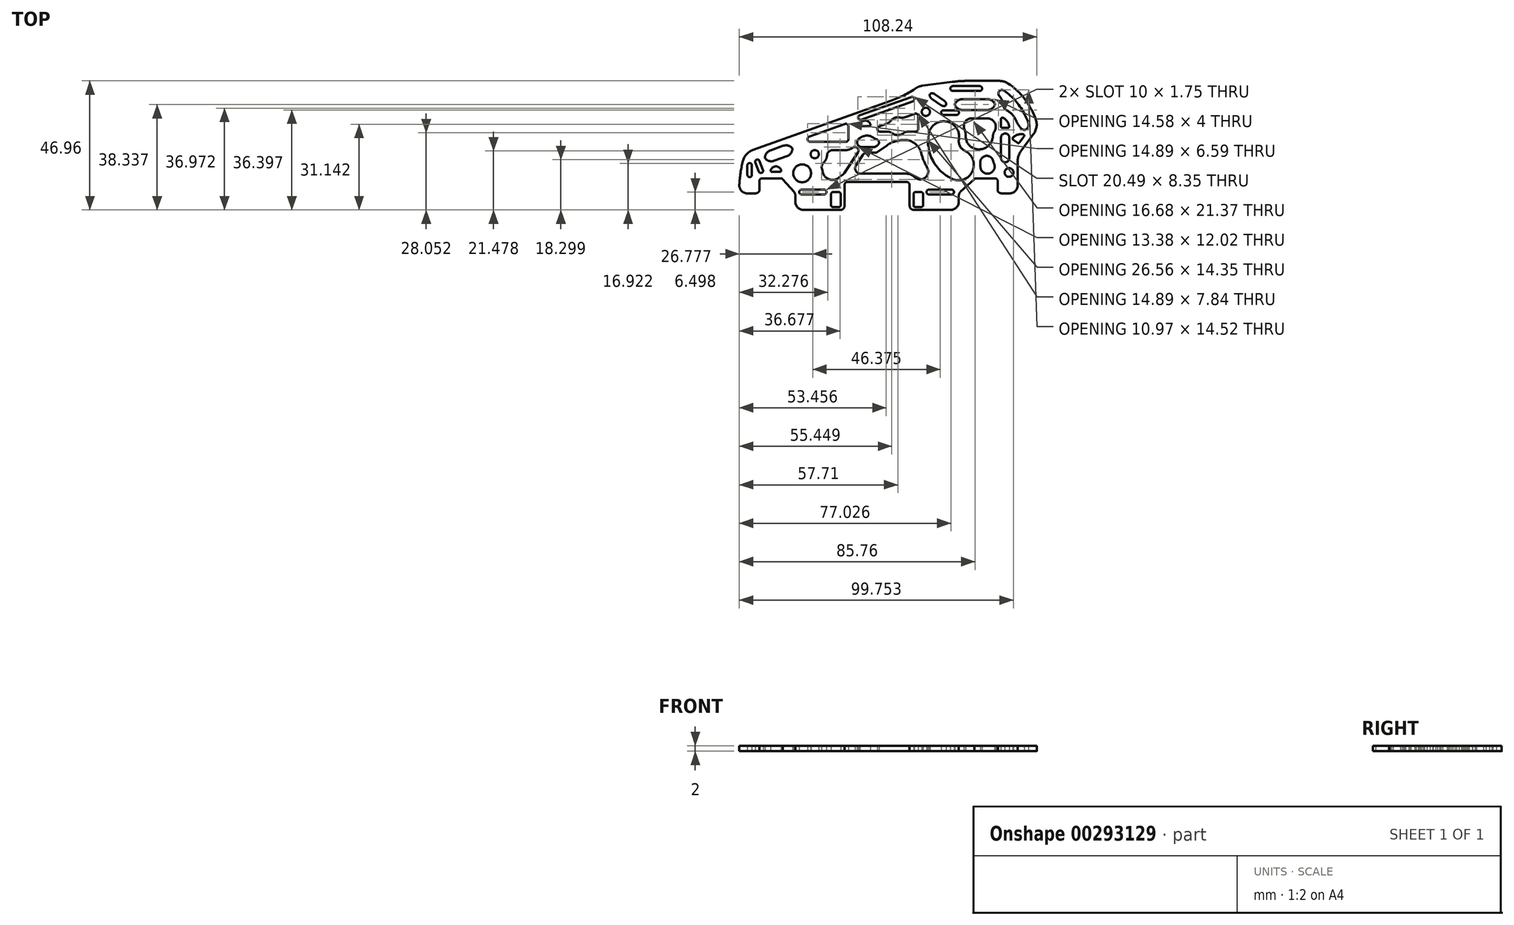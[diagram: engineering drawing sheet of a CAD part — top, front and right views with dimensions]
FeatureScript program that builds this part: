
annotation { "Feature Type Name" : "Feature", "Feature Type Description" : "" }
export const myFeature = defineFeature(function(context is Context, id is Id, definition is map)
    precondition{}
    {
        {
            var Q0;
            Q0=qCreatedBy(makeId("Top.planeOp"),FACE);
            var sketch = newSketch(context, id + "F0", { "sketchPlane" : qUnion([Q0])});
            skArc(sketch, "E0", {"start": v(29.13, 23.48) * mm, "mid": v(26.3, 23.4) * mm, "end": v(23.48, 23.12) * mm});
            skLineSegment(sketch, "E1", {"start": v(0.85, 16.15) * mm, "end": v(-49.03, -1.6) * mm});
            skArc(sketch, "E2", {"start": v(-49.03, -1.6) * mm, "mid": v(-51.49, -3.25) * mm, "end": v(-52.86, -5.87) * mm});
            skArc(sketch, "E3", {"start": v(-52.86, -5.87) * mm, "mid": v(-53.67, -10.05) * mm, "end": v(-54.12, -14.3) * mm});
            skArc(sketch, "E4", {"start": v(-54.12, -14.3) * mm, "mid": v(-53.31, -16.53) * mm, "end": v(-51.12, -17.48) * mm});
            skLineSegment(sketch, "E5", {"start": v(-51.12, -17.48) * mm, "end": v(-48.44, -17.48) * mm});
            skArc(sketch, "E6", {"start": v(-48.44, -17.48) * mm, "mid": v(-47.78, -17.37) * mm, "end": v(-47.2, -17.05) * mm});
            skArc(sketch, "E7", {"start": v(-47.2, -17.05) * mm, "mid": v(-46.92, -16.7) * mm, "end": v(-46.82, -16.27) * mm});
            skLineSegment(sketch, "E8", {"start": v(-46.82, -16.27) * mm, "end": v(-46.82, -12.98) * mm});
            skArc(sketch, "E9", {"start": v(-45.82, -11.98) * mm, "mid": v(-46.53, -12.27) * mm, "end": v(-46.82, -12.98) * mm});
            skLineSegment(sketch, "E10", {"start": v(-45.82, -11.98) * mm, "end": v(-39.02, -11.98) * mm});
            skArc(sketch, "E11", {"start": v(-38.23, -12.37) * mm, "mid": v(-38.58, -12.08) * mm, "end": v(-39.02, -11.98) * mm});
            skArc(sketch, "E12", {"start": v(-33.72, -20.48) * mm, "mid": v(-32.84, -22.6) * mm, "end": v(-30.72, -23.48) * mm});
            skLineSegment(sketch, "E13", {"start": v(-30.72, -23.48) * mm, "end": v(-17.32, -23.48) * mm});
            skArc(sketch, "E14", {"start": v(22.78, -23.48) * mm, "mid": v(24.9, -22.6) * mm, "end": v(25.78, -20.48) * mm});
            skLineSegment(sketch, "E15", {"start": v(25.78, -20.48) * mm, "end": v(25.78, -18.36) * mm});
            skArc(sketch, "E16", {"start": v(32.11, -11.98) * mm, "mid": v(31.73, -12.06) * mm, "end": v(31.4, -12.27) * mm});
            skLineSegment(sketch, "E17", {"start": v(32.11, -11.98) * mm, "end": v(38.91, -11.98) * mm});
            skArc(sketch, "E18", {"start": v(39.91, -12.98) * mm, "mid": v(39.62, -12.27) * mm, "end": v(38.91, -11.98) * mm});
            skLineSegment(sketch, "E19", {"start": v(39.91, -12.98) * mm, "end": v(39.91, -16.65) * mm});
            skArc(sketch, "E20", {"start": v(39.91, -16.65) * mm, "mid": v(40.62, -17.26) * mm, "end": v(41.53, -17.48) * mm});
            skLineSegment(sketch, "E21", {"start": v(41.53, -17.48) * mm, "end": v(44.2, -17.48) * mm});
            skArc(sketch, "E22", {"start": v(44.2, -17.48) * mm, "mid": v(46.32, -16.6) * mm, "end": v(47.2, -14.48) * mm});
            skLineSegment(sketch, "E23", {"start": v(47.2, -14.48) * mm, "end": v(47.2, -5.72) * mm});
            skArc(sketch, "E24", {"start": v(-47.04, -9.52) * mm, "mid": v(-45.98, -10) * mm, "end": v(-45.5, -8.94) * mm});
            skLineSegment(sketch, "E25", {"start": v(-48.27, -6.25) * mm, "end": v(-47.04, -9.52) * mm});
            skArc(sketch, "E26", {"start": v(-46.73, -5.66) * mm, "mid": v(-47.8, -5.18) * mm, "end": v(-48.27, -6.25) * mm});
            skLineSegment(sketch, "E27", {"start": v(-45.5, -8.94) * mm, "end": v(-46.73, -5.66) * mm});
            skCircle(sketch, "E28", {"center": v(-26.66, -3.2) * mm, "radius": 1.5 * mm});
            skCircle(sketch, "E29", {"center": v(13.78, 12.22) * mm, "radius": 1.5 * mm});
            skArc(sketch, "E30", {"start": v(-34.78, -1.3) * mm, "mid": v(-34.81, -1.1) * mm, "end": v(-34.92, -0.92) * mm});
            skArc(sketch, "E31", {"start": v(-36.77, -3.92) * mm, "mid": v(-35.39, -2.9) * mm, "end": v(-34.78, -1.3) * mm});
            skLineSegment(sketch, "E32", {"start": v(-41.48, -5.6) * mm, "end": v(-36.77, -3.92) * mm});
            skArc(sketch, "E33", {"start": v(-44.68, -4.82) * mm, "mid": v(-43.2, -5.69) * mm, "end": v(-41.48, -5.6) * mm});
            skArc(sketch, "E34", {"start": v(-44.8, -4.44) * mm, "mid": v(-44.78, -4.65) * mm, "end": v(-44.68, -4.82) * mm});
            skArc(sketch, "E35", {"start": v(-42.82, -1.83) * mm, "mid": v(-44.2, -2.84) * mm, "end": v(-44.8, -4.44) * mm});
            skLineSegment(sketch, "E36", {"start": v(-38.11, -0.15) * mm, "end": v(-42.82, -1.83) * mm});
            skArc(sketch, "E37", {"start": v(-34.92, -0.92) * mm, "mid": v(-36.4, -0.06) * mm, "end": v(-38.11, -0.15) * mm});
            skLineSegment(sketch, "E38", {"start": v(27.14, 12.86) * mm, "end": v(36.14, 12.86) * mm});
            skArc(sketch, "E39", {"start": v(24.4, 14.66) * mm, "mid": v(25.5, 13.35) * mm, "end": v(27.14, 12.86) * mm});
            skArc(sketch, "E40", {"start": v(24.4, 15.06) * mm, "mid": v(24.35, 14.86) * mm, "end": v(24.4, 14.66) * mm});
            skArc(sketch, "E41", {"start": v(27.14, 16.86) * mm, "mid": v(25.5, 16.37) * mm, "end": v(24.4, 15.06) * mm});
            skLineSegment(sketch, "E42", {"start": v(36.14, 16.86) * mm, "end": v(27.14, 16.86) * mm});
            skArc(sketch, "E43", {"start": v(38.89, 15.06) * mm, "mid": v(37.78, 16.37) * mm, "end": v(36.14, 16.86) * mm});
            skArc(sketch, "E44", {"start": v(38.89, 14.66) * mm, "mid": v(38.93, 14.86) * mm, "end": v(38.89, 15.06) * mm});
            skArc(sketch, "E45", {"start": v(36.14, 12.86) * mm, "mid": v(37.78, 13.35) * mm, "end": v(38.89, 14.66) * mm});
            skArc(sketch, "E46", {"start": v(-15.4, 1.28) * mm, "mid": v(-14.7, 1.57) * mm, "end": v(-14.4, 2.28) * mm});
            skLineSegment(sketch, "E47", {"start": v(-28.3, 1.28) * mm, "end": v(-15.4, 1.28) * mm});
            skArc(sketch, "E48", {"start": v(-28.64, 3.22) * mm, "mid": v(-29.29, 2.1) * mm, "end": v(-28.3, 1.28) * mm});
            skLineSegment(sketch, "E49", {"start": v(-15.74, 7.81) * mm, "end": v(-28.64, 3.22) * mm});
            skArc(sketch, "E50", {"start": v(-14.4, 6.87) * mm, "mid": v(-14.82, 7.69) * mm, "end": v(-15.74, 7.81) * mm});
            skLineSegment(sketch, "E51", {"start": v(-14.4, 2.28) * mm, "end": v(-14.4, 6.87) * mm});
            skLineSegment(sketch, "E52", {"start": v(-19.97, -22.48) * mm, "end": v(-17.97, -22.48) * mm});
            skArc(sketch, "E53", {"start": v(-20.72, -21.73) * mm, "mid": v(-20.5, -22.26) * mm, "end": v(-19.97, -22.48) * mm});
            skLineSegment(sketch, "E54", {"start": v(-20.72, -17.73) * mm, "end": v(-20.72, -21.73) * mm});
            skArc(sketch, "E55", {"start": v(-19.97, -16.98) * mm, "mid": v(-20.5, -17.2) * mm, "end": v(-20.72, -17.73) * mm});
            skLineSegment(sketch, "E56", {"start": v(-17.97, -16.98) * mm, "end": v(-19.97, -16.98) * mm});
            skArc(sketch, "E57", {"start": v(-17.22, -17.73) * mm, "mid": v(-17.44, -17.2) * mm, "end": v(-17.97, -16.98) * mm});
            skLineSegment(sketch, "E58", {"start": v(-17.22, -21.73) * mm, "end": v(-17.22, -17.73) * mm});
            skArc(sketch, "E59", {"start": v(-17.97, -22.48) * mm, "mid": v(-17.44, -22.26) * mm, "end": v(-17.22, -21.73) * mm});
            skArc(sketch, "E60", {"start": v(14.9, -16.1) * mm, "mid": v(14.03, -16.98) * mm, "end": v(14.9, -17.86) * mm});
            skLineSegment(sketch, "E61", {"start": v(23.16, -16.1) * mm, "end": v(14.9, -16.1) * mm});
            skArc(sketch, "E62", {"start": v(23.16, -17.86) * mm, "mid": v(24.03, -16.98) * mm, "end": v(23.16, -16.1) * mm});
            skLineSegment(sketch, "E63", {"start": v(14.9, -17.86) * mm, "end": v(23.16, -17.86) * mm});
            skArc(sketch, "E64", {"start": v(-31.47, -16.1) * mm, "mid": v(-32.34, -16.98) * mm, "end": v(-31.47, -17.86) * mm});
            skLineSegment(sketch, "E65", {"start": v(-23.22, -16.1) * mm, "end": v(-31.47, -16.1) * mm});
            skArc(sketch, "E66", {"start": v(-23.22, -17.86) * mm, "mid": v(-22.34, -16.98) * mm, "end": v(-23.22, -16.1) * mm});
            skLineSegment(sketch, "E67", {"start": v(-31.47, -17.86) * mm, "end": v(-23.22, -17.86) * mm});
            skCircle(sketch, "E68", {"center": v(-31.24, -10.14) * mm, "radius": 3.25 * mm});
            skCircle(sketch, "E69", {"center": v(44.08, -9.86) * mm, "radius": 1.6 * mm});
            skLineSegment(sketch, "E70", {"start": v(6.78, -13.3) * mm, "end": v(-14.72, -13.3) * mm});
            skArc(sketch, "E71", {"start": v(7.88, -14.4) * mm, "mid": v(7.56, -13.63) * mm, "end": v(6.78, -13.3) * mm});
            skArc(sketch, "E72", {"start": v(-14.72, -13.3) * mm, "mid": v(-15.5, -13.63) * mm, "end": v(-15.82, -14.4) * mm});
            skLineSegment(sketch, "E73", {"start": v(10.03, -22.48) * mm, "end": v(12.03, -22.48) * mm});
            skArc(sketch, "E74", {"start": v(9.28, -21.73) * mm, "mid": v(9.5, -22.26) * mm, "end": v(10.03, -22.48) * mm});
            skLineSegment(sketch, "E75", {"start": v(9.28, -17.73) * mm, "end": v(9.28, -21.73) * mm});
            skArc(sketch, "E76", {"start": v(10.03, -16.98) * mm, "mid": v(9.5, -17.2) * mm, "end": v(9.28, -17.73) * mm});
            skLineSegment(sketch, "E77", {"start": v(12.03, -16.98) * mm, "end": v(10.03, -16.98) * mm});
            skArc(sketch, "E78", {"start": v(12.78, -17.73) * mm, "mid": v(12.56, -17.2) * mm, "end": v(12.03, -16.98) * mm});
            skLineSegment(sketch, "E79", {"start": v(12.78, -21.73) * mm, "end": v(12.78, -17.73) * mm});
            skArc(sketch, "E80", {"start": v(12.03, -22.48) * mm, "mid": v(12.56, -22.26) * mm, "end": v(12.78, -21.73) * mm});
            skLineSegment(sketch, "E81", {"start": v(41.64, 6.36) * mm, "end": v(43.6, 6.36) * mm});
            skArc(sketch, "E82", {"start": v(41.14, 6.86) * mm, "mid": v(41.29, 6.5) * mm, "end": v(41.64, 6.36) * mm});
            skLineSegment(sketch, "E83", {"start": v(41.14, 9.62) * mm, "end": v(41.14, 6.86) * mm});
            skArc(sketch, "E84", {"start": v(41.87, 10.07) * mm, "mid": v(41.38, 10.05) * mm, "end": v(41.14, 9.62) * mm});
            skArc(sketch, "E85", {"start": v(44.1, 6.92) * mm, "mid": v(43.37, 8.77) * mm, "end": v(41.87, 10.07) * mm});
            skArc(sketch, "E86", {"start": v(43.6, 6.36) * mm, "mid": v(43.98, 6.53) * mm, "end": v(44.1, 6.92) * mm});
            skLineSegment(sketch, "E87", {"start": v(41.14, 2.86) * mm, "end": v(41.14, -4.64) * mm});
            skArc(sketch, "E88", {"start": v(44.14, 2.86) * mm, "mid": v(42.64, 4.36) * mm, "end": v(41.14, 2.86) * mm});
            skLineSegment(sketch, "E89", {"start": v(44.14, -4.64) * mm, "end": v(44.14, 2.86) * mm});
            skArc(sketch, "E90", {"start": v(41.14, -4.64) * mm, "mid": v(42.64, -6.14) * mm, "end": v(44.14, -4.64) * mm});
            skLineSegment(sketch, "E91", {"start": v(-9.8, 9.36) * mm, "end": v(9.03, 16.07) * mm});
            skArc(sketch, "E92", {"start": v(-10.36, 10.92) * mm, "mid": v(-10.86, 9.86) * mm, "end": v(-9.8, 9.36) * mm});
            skLineSegment(sketch, "E93", {"start": v(8.48, 17.62) * mm, "end": v(-10.36, 10.92) * mm});
            skArc(sketch, "E94", {"start": v(9.03, 16.07) * mm, "mid": v(9.53, 17.12) * mm, "end": v(8.48, 17.62) * mm});
            skLineSegment(sketch, "E95", {"start": v(23.58, 19.82) * mm, "end": v(33.38, 19.82) * mm});
            skLineSegment(sketch, "E96", {"start": v(33.38, 21.57) * mm, "end": v(23.58, 21.57) * mm});
            skLineSegment(sketch, "E97", {"start": v(7.33, 5) * mm, "end": v(10.03, 5) * mm});
            skArc(sketch, "E98", {"start": v(-3.2, 6.94) * mm, "mid": v(-3.85, 5.82) * mm, "end": v(-2.87, 5) * mm});
            skLineSegment(sketch, "E99", {"start": v(9.7, 11.53) * mm, "end": v(6.07, 10.24) * mm});
            skArc(sketch, "E100", {"start": v(11.03, 10.59) * mm, "mid": v(10.61, 11.4) * mm, "end": v(9.7, 11.53) * mm});
            skLineSegment(sketch, "E101", {"start": v(11.03, 6) * mm, "end": v(11.03, 10.59) * mm});
            skArc(sketch, "E102", {"start": v(10.03, 5) * mm, "mid": v(10.74, 5.29) * mm, "end": v(11.03, 6) * mm});
            skLineSegment(sketch, "E103", {"start": v(-33.72, -18.24) * mm, "end": v(-33.72, -20.48) * mm});
            skLineSegment(sketch, "E104", {"start": v(-34.22, -16.91) * mm, "end": v(-38.23, -12.37) * mm});
            skArc(sketch, "E105", {"start": v(-33.72, -18.24) * mm, "mid": v(-33.85, -17.53) * mm, "end": v(-34.22, -16.91) * mm});
            skLineSegment(sketch, "E106", {"start": v(26.42, -16.89) * mm, "end": v(31.4, -12.27) * mm});
            skArc(sketch, "E107", {"start": v(26.42, -16.89) * mm, "mid": v(25.95, -17.55) * mm, "end": v(25.78, -18.36) * mm});
            skArc(sketch, "E108", {"start": v(-49.53, -7.24) * mm, "mid": v(-50.35, -6.41) * mm, "end": v(-51.18, -7.24) * mm});
            skLineSegment(sketch, "E109", {"start": v(-51.18, -10.74) * mm, "end": v(-51.18, -7.24) * mm});
            skArc(sketch, "E110", {"start": v(-51.18, -10.74) * mm, "mid": v(-50.35, -11.56) * mm, "end": v(-49.53, -10.74) * mm});
            skLineSegment(sketch, "E111", {"start": v(-49.53, -7.24) * mm, "end": v(-49.53, -10.74) * mm});
            skLineSegment(sketch, "E112", {"start": v(7.88, -14.4) * mm, "end": v(7.88, -21.98) * mm});
            skLineSegment(sketch, "E113", {"start": v(-15.82, -21.98) * mm, "end": v(-15.82, -14.4) * mm});
            skArc(sketch, "E114", {"start": v(-17.32, -23.48) * mm, "mid": v(-16.26, -23.04) * mm, "end": v(-15.82, -21.98) * mm});
            skLineSegment(sketch, "E115", {"start": v(9.38, -23.48) * mm, "end": v(22.78, -23.48) * mm});
            skArc(sketch, "E116", {"start": v(7.88, -21.98) * mm, "mid": v(8.32, -23.04) * mm, "end": v(9.38, -23.48) * mm});
            skLineSegment(sketch, "E117", {"start": v(23.48, 23.12) * mm, "end": v(12.54, 21.72) * mm});
            skArc(sketch, "E118", {"start": v(0.85, 16.15) * mm, "mid": v(5.78, 18.25) * mm, "end": v(10.42, 20.93) * mm});
            skArc(sketch, "E119", {"start": v(12.54, 21.72) * mm, "mid": v(11.43, 21.45) * mm, "end": v(10.42, 20.93) * mm});
            skArc(sketch, "E120", {"start": v(52.6, 12.21) * mm, "mid": v(48.93, 17.92) * mm, "end": v(43.88, 22.44) * mm});
            skLineSegment(sketch, "E121", {"start": v(48.37, -2.16) * mm, "end": v(52.95, 4.04) * mm});
            skArc(sketch, "E122", {"start": v(48.37, -2.16) * mm, "mid": v(47.5, -3.84) * mm, "end": v(47.2, -5.72) * mm});
            skLineSegment(sketch, "E123", {"start": v(40.51, 23.48) * mm, "end": v(29.13, 23.48) * mm});
            skArc(sketch, "E124", {"start": v(43.88, 22.44) * mm, "mid": v(42.28, 23.22) * mm, "end": v(40.51, 23.48) * mm});
            skLineSegment(sketch, "E125", {"start": v(53.56, 10.14) * mm, "end": v(52.6, 12.21) * mm});
            skArc(sketch, "E126", {"start": v(52.95, 4.04) * mm, "mid": v(54.1, 7) * mm, "end": v(53.56, 10.14) * mm});
            skArc(sketch, "E127", {"start": v(48.55, 6.1) * mm, "mid": v(49.9, 5.69) * mm, "end": v(50.96, 6.62) * mm});
            skArc(sketch, "E128", {"start": v(50.96, 6.62) * mm, "mid": v(51.12, 7.76) * mm, "end": v(50.84, 8.87) * mm});
            skLineSegment(sketch, "E129", {"start": v(49.88, 10.94) * mm, "end": v(50.84, 8.87) * mm});
            skArc(sketch, "E130", {"start": v(49.88, 10.94) * mm, "mid": v(46.65, 15.97) * mm, "end": v(42.2, 19.96) * mm});
            skArc(sketch, "E131", {"start": v(42.2, 19.96) * mm, "mid": v(40.46, 19.73) * mm, "end": v(40.5, 17.97) * mm});
            skArc(sketch, "E132", {"start": v(41.64, 16.26) * mm, "mid": v(41.15, 17.16) * mm, "end": v(40.5, 17.97) * mm});
            skArc(sketch, "E133", {"start": v(41.93, 14.86) * mm, "mid": v(41.86, 15.57) * mm, "end": v(41.64, 16.26) * mm});
            skArc(sketch, "E134", {"start": v(41.93, 14.86) * mm, "mid": v(42.28, 13.62) * mm, "end": v(43.23, 12.74) * mm});
            skArc(sketch, "E135", {"start": v(46.58, 9.13) * mm, "mid": v(45.23, 11.23) * mm, "end": v(43.23, 12.74) * mm});
            skArc(sketch, "E136", {"start": v(46.58, 9.13) * mm, "mid": v(47.43, 7.53) * mm, "end": v(48.55, 6.1) * mm});
            skArc(sketch, "E137", {"start": v(49.16, 4.05) * mm, "mid": v(47.18, 3.9) * mm, "end": v(45.5, 2.85) * mm});
            skArc(sketch, "E138", {"start": v(49.48, 3.26) * mm, "mid": v(49.54, 3.74) * mm, "end": v(49.16, 4.05) * mm});
            skLineSegment(sketch, "E139", {"start": v(47.84, 1.03) * mm, "end": v(49.48, 3.26) * mm});
            skArc(sketch, "E140", {"start": v(47.14, 0.93) * mm, "mid": v(47.51, 0.84) * mm, "end": v(47.84, 1.03) * mm});
            skLineSegment(sketch, "E141", {"start": v(45.56, 2.1) * mm, "end": v(47.14, 0.93) * mm});
            skArc(sketch, "E142", {"start": v(45.5, 2.85) * mm, "mid": v(45.36, 2.46) * mm, "end": v(45.56, 2.1) * mm});
            skLineSegment(sketch, "E143", {"start": v(30.45, 9.86) * mm, "end": v(36.14, 9.86) * mm});
            skArc(sketch, "E144", {"start": v(30.45, 9.86) * mm, "mid": v(28.1, 8.63) * mm, "end": v(27.79, 6) * mm});
            skArc(sketch, "E145", {"start": v(28.31, 3.17) * mm, "mid": v(28.18, 4.61) * mm, "end": v(27.79, 6) * mm});
            skArc(sketch, "E146", {"start": v(28.31, 3.17) * mm, "mid": v(28.82, 1.08) * mm, "end": v(30.24, -0.54) * mm});
            skArc(sketch, "E147", {"start": v(30.24, -0.54) * mm, "mid": v(35.28, -0.97) * mm, "end": v(38.15, 3.2) * mm});
            skArc(sketch, "E148", {"start": v(38.78, 5.18) * mm, "mid": v(38.35, 4.23) * mm, "end": v(38.15, 3.2) * mm});
            skArc(sketch, "E149", {"start": v(38.78, 5.18) * mm, "mid": v(38.83, 8.29) * mm, "end": v(36.14, 9.86) * mm});
            skArc(sketch, "E150", {"start": v(25.83, 2.2) * mm, "mid": v(26.2, -0.28) * mm, "end": v(28.02, -2.02) * mm});
            skArc(sketch, "E151", {"start": v(25.83, 2.2) * mm, "mid": v(21.28, 8.68) * mm, "end": v(14.8, 4.14) * mm});
            skArc(sketch, "E152", {"start": v(14.8, 4.14) * mm, "mid": v(16.27, -5.45) * mm, "end": v(23.28, -12.17) * mm});
            skArc(sketch, "E153", {"start": v(23.28, -12.17) * mm, "mid": v(30.73, -9.46) * mm, "end": v(28.02, -2.02) * mm});
            skArc(sketch, "E154", {"start": v(33.64, -7.55) * mm, "mid": v(33.65, -6.96) * mm, "end": v(33.62, -6.37) * mm});
            skArc(sketch, "E155", {"start": v(33.64, -7.55) * mm, "mid": v(36.73, -10.25) * mm, "end": v(38.58, -6.58) * mm});
            skArc(sketch, "E156", {"start": v(38.25, -5.64) * mm, "mid": v(38.39, -6.12) * mm, "end": v(38.58, -6.58) * mm});
            skArc(sketch, "E157", {"start": v(38.25, -5.64) * mm, "mid": v(35.6, -3.83) * mm, "end": v(33.62, -6.37) * mm});
            skArc(sketch, "E158", {"start": v(-5.2, 2.74) * mm, "mid": v(-8.07, 3.53) * mm, "end": v(-10.76, 2.24) * mm});
            skArc(sketch, "E159", {"start": v(-10.76, 2.24) * mm, "mid": v(-11.1, 0.43) * mm, "end": v(-9.56, -0.6) * mm});
            skLineSegment(sketch, "E160", {"start": v(-4.87, -0.6) * mm, "end": v(-9.56, -0.6) * mm});
            skArc(sketch, "E161", {"start": v(-4.87, -0.6) * mm, "mid": v(-4.72, -0.57) * mm, "end": v(-4.58, -0.5) * mm});
            skLineSegment(sketch, "E162", {"start": v(-3.77, 0.07) * mm, "end": v(-4.58, -0.5) * mm});
            skArc(sketch, "E163", {"start": v(-3.77, 0.07) * mm, "mid": v(-3.28, 1.23) * mm, "end": v(-4.1, 2.19) * mm});
            skArc(sketch, "E164", {"start": v(-5.2, 2.74) * mm, "mid": v(-4.67, 2.42) * mm, "end": v(-4.1, 2.19) * mm});
            skLineSegment(sketch, "E165", {"start": v(-10.96, -2.6) * mm, "end": v(-15.99, -10.16) * mm});
            skArc(sketch, "E166", {"start": v(-10.96, -2.6) * mm, "mid": v(-11.17, -0.89) * mm, "end": v(-12.9, -0.84) * mm});
            skArc(sketch, "E167", {"start": v(-15.4, -1.72) * mm, "mid": v(-14.07, -1.5) * mm, "end": v(-12.9, -0.84) * mm});
            skLineSegment(sketch, "E168", {"start": v(-20.18, -1.72) * mm, "end": v(-15.4, -1.72) * mm});
            skArc(sketch, "E169", {"start": v(-20.18, -1.72) * mm, "mid": v(-21.54, -2.25) * mm, "end": v(-22.17, -3.56) * mm});
            skArc(sketch, "E170", {"start": v(-23.53, -6.44) * mm, "mid": v(-22.59, -5.12) * mm, "end": v(-22.17, -3.56) * mm});
            skArc(sketch, "E171", {"start": v(-23.53, -6.44) * mm, "mid": v(-24.08, -7.42) * mm, "end": v(-24.02, -8.54) * mm});
            skArc(sketch, "E172", {"start": v(-23.79, -9.47) * mm, "mid": v(-23.88, -9) * mm, "end": v(-24.02, -8.54) * mm});
            skArc(sketch, "E173", {"start": v(-23.79, -9.47) * mm, "mid": v(-21.33, -12.39) * mm, "end": v(-17.62, -11.5) * mm});
            skArc(sketch, "E174", {"start": v(-16.69, -10.81) * mm, "mid": v(-17.18, -11.13) * mm, "end": v(-17.62, -11.5) * mm});
            skArc(sketch, "E175", {"start": v(-16.69, -10.81) * mm, "mid": v(-16.3, -10.53) * mm, "end": v(-15.99, -10.16) * mm});
            skArc(sketch, "E176", {"start": v(17.1, 18.6) * mm, "mid": v(16.52, 18.89) * mm, "end": v(15.87, 18.97) * mm});
            skLineSegment(sketch, "E177", {"start": v(20.38, 16.31) * mm, "end": v(17.1, 18.6) * mm});
            skArc(sketch, "E178", {"start": v(21.14, 15.28) * mm, "mid": v(20.85, 15.86) * mm, "end": v(20.38, 16.31) * mm});
            skArc(sketch, "E179", {"start": v(20.47, 14.31) * mm, "mid": v(21.04, 14.63) * mm, "end": v(21.14, 15.28) * mm});
            skArc(sketch, "E180", {"start": v(19.24, 14.67) * mm, "mid": v(19.82, 14.4) * mm, "end": v(20.47, 14.31) * mm});
            skLineSegment(sketch, "E181", {"start": v(15.96, 16.97) * mm, "end": v(19.24, 14.67) * mm});
            skArc(sketch, "E182", {"start": v(15.2, 18) * mm, "mid": v(15.5, 17.42) * mm, "end": v(15.96, 16.97) * mm});
            skArc(sketch, "E183", {"start": v(15.87, 18.97) * mm, "mid": v(15.3, 18.65) * mm, "end": v(15.2, 18) * mm});
            skLineSegment(sketch, "E184", {"start": v(-7.5, -2.6) * mm, "end": v(-4.23, -2.6) * mm});
            skArc(sketch, "E185", {"start": v(-7.5, -2.6) * mm, "mid": v(-8.44, -2.83) * mm, "end": v(-9.16, -3.49) * mm});
            skLineSegment(sketch, "E186", {"start": v(-11.62, -7.2) * mm, "end": v(-9.16, -3.49) * mm});
            skArc(sketch, "E187", {"start": v(-11.62, -7.2) * mm, "mid": v(-11.72, -9.25) * mm, "end": v(-9.95, -10.3) * mm});
            skLineSegment(sketch, "E188", {"start": v(6.78, -10.3) * mm, "end": v(-9.95, -10.3) * mm});
            skArc(sketch, "E189", {"start": v(9.68, -11.5) * mm, "mid": v(8.35, -10.62) * mm, "end": v(6.78, -10.3) * mm});
            skArc(sketch, "E190", {"start": v(9.68, -11.5) * mm, "mid": v(13.54, -11.74) * mm, "end": v(14.23, -7.93) * mm});
            skArc(sketch, "E191", {"start": v(12.1, -2.81) * mm, "mid": v(12.96, -5.45) * mm, "end": v(14.23, -7.93) * mm});
            skArc(sketch, "E192", {"start": v(12.1, -2.81) * mm, "mid": v(9.85, 0.65) * mm, "end": v(5.96, 2) * mm});
            skArc(sketch, "E193", {"start": v(5.96, 2) * mm, "mid": v(2.58, 1.47) * mm, "end": v(-0.49, -0.06) * mm});
            skLineSegment(sketch, "E194", {"start": v(-3.94, -2.5) * mm, "end": v(-0.49, -0.06) * mm});
            skArc(sketch, "E195", {"start": v(-4.23, -2.6) * mm, "mid": v(-4.08, -2.57) * mm, "end": v(-3.94, -2.5) * mm});
            skLineSegment(sketch, "E196", {"start": v(-42.2, -9.63) * mm, "end": v(-39.36, -9.63) * mm});
            skArc(sketch, "E197", {"start": v(-42.66, -8.97) * mm, "mid": v(-42.6, -9.42) * mm, "end": v(-42.2, -9.63) * mm});
            skArc(sketch, "E198", {"start": v(-38.9, -8.97) * mm, "mid": v(-40.78, -7.63) * mm, "end": v(-42.66, -8.97) * mm});
            skArc(sketch, "E199", {"start": v(-39.36, -9.63) * mm, "mid": v(-38.95, -9.42) * mm, "end": v(-38.9, -8.97) * mm});
            skLineSegment(sketch, "E200", {"start": v(-9.71, 7.04) * mm, "end": v(-6.88, 7.04) * mm});
            skArc(sketch, "E201", {"start": v(-10.18, 7.7) * mm, "mid": v(-10.12, 7.25) * mm, "end": v(-9.71, 7.04) * mm});
            skArc(sketch, "E202", {"start": v(-6.41, 7.7) * mm, "mid": v(-8.3, 9.04) * mm, "end": v(-10.18, 7.7) * mm});
            skArc(sketch, "E203", {"start": v(-6.88, 7.04) * mm, "mid": v(-6.47, 7.25) * mm, "end": v(-6.41, 7.7) * mm});
            skArc(sketch, "E204", {"start": v(20.18, 12.79) * mm, "mid": v(19.33, 11.94) * mm, "end": v(20.18, 11.09) * mm});
            skLineSegment(sketch, "E205", {"start": v(24.98, 12.79) * mm, "end": v(20.18, 12.79) * mm});
            skArc(sketch, "E206", {"start": v(24.98, 11.09) * mm, "mid": v(25.83, 11.94) * mm, "end": v(24.98, 12.79) * mm});
            skLineSegment(sketch, "E207", {"start": v(20.18, 11.09) * mm, "end": v(24.98, 11.09) * mm});
            skArc(sketch, "E208", {"start": v(23.58, 21.57) * mm, "mid": v(22.7, 20.7) * mm, "end": v(23.58, 19.82) * mm});
            skArc(sketch, "E209", {"start": v(33.38, 19.82) * mm, "mid": v(34.26, 20.7) * mm, "end": v(33.38, 21.57) * mm});
            skArc(sketch, "E210", {"start": v(1.63, 4.4) * mm, "mid": v(3.58, 3.74) * mm, "end": v(5.53, 4.4) * mm});
            skArc(sketch, "E211", {"start": v(4.35, 10.15) * mm, "mid": v(2.5, 10.06) * mm, "end": v(0.99, 8.95) * mm});
            skLineSegment(sketch, "E212", {"start": v(-0.4, 7.93) * mm, "end": v(-3.2, 6.94) * mm});
            skLineSegment(sketch, "E213", {"start": v(-2.87, 5) * mm, "end": v(-0.17, 5) * mm});
            skArc(sketch, "E214", {"start": v(-0.4, 7.93) * mm, "mid": v(0.37, 8.34) * mm, "end": v(0.99, 8.95) * mm});
            skArc(sketch, "E215", {"start": v(4.35, 10.15) * mm, "mid": v(5.22, 10.07) * mm, "end": v(6.07, 10.24) * mm});
            skArc(sketch, "E216", {"start": v(7.33, 5) * mm, "mid": v(6.38, 4.84) * mm, "end": v(5.53, 4.4) * mm});
            skArc(sketch, "E217", {"start": v(1.63, 4.4) * mm, "mid": v(0.78, 4.84) * mm, "end": v(-0.17, 5) * mm});
            skSolve(sketch);
        }
        {
            var Q0;
            Q0 = qSketchRegion(id + "F0", true);
            extrude(context, id + "F1", {"entities" : qUnion([Q0]), "depth" : 2 * mm});
        }
    });
